# Revit family: linedo_2_3m_30_1100_952330_832_776_503_7247
name_source: partatom
category: Lighting Fixtures
units: mm (PartAtom-declared; Revit-internal decimal feet)

## family parameters
Cut with Voids When Loaded = No
Host = Face
Light Source = No
Part Type = Normal
Room Calculation Point = No
Round Connector Dimension = Use Diameter
Shared = No

## types (1)
- LINEDO_2,3m_30_1100 (1 x LED Modul 830, 3900 lm, 3000)
    Apparent Load = 54 VA
    CIE Flux Codes = 89 97 99 100 100
    Color Rendering = 80
    Color Temperature = 3000
    Default Elevation = 1800 mm
    Description = LINEDO, 54 W, 7800 lm, 830, white, DALI
Continuous line luminaire, L 2291 B 58 H 76
    Height = 76 mm
    Lamp = 1 x LED Modul 830
    Lamp Light Flux = 3900 lm
    Lamp count = 1
    Length = 2291 mm
    Lifetime = 50000 h
    Luminous efficacy = 144 lm/W
    Manufacturer = RZB
    ModVariant = No
    Model = 952330.832.776.503
    Mounting Place = Ceiling
    Mounting Type = Surface mounted, Pendant
    Number of Poles = 1
    OnlyDefault = Yes
    Power Factor = 1
    Product Name = LINEDO_2,3m_30_1100
    Product group = Surface mounted continuous line luminaire system
    ProductGroupID = 310
    Protection Class = Protection class I
    Protection Degree = IP 54
    RLX_Detail_Level = 1
    RLX_Emergency_Light_Flux = 0 lm
    RLX_Emergency_Type = 0
    RLX_Emergency_Type_DB = No
    RlxData = <blob elided: 44573 chars, md5=cd4af72f>
    Socket = socket
    Standby Power = 0 W
    System Light Flux = 7800 lm
    System Power = 54 W
    Type Comments = Product without accessories
    Type Image = 954530.852.476.504.jpg
    URL = http://relux.com
    VarID = ---
    Voltage = 230 V
    Voltage Range = 220-240 V
    Weight = 0.00 kg
    Width = 58 mm

## geometry (parser evidence)
native form markers: Sweep x12
no freeform markers — native parametric forms only
